# Revit family: 305_40080496f50843ed95814908d8aeb8
name_source: partatom
category: Pipe Accessories
revit_build: Autodesk Revit 2018 (Build: 20170223_1515(x64)
units: mm (PartAtom-declared; Revit-internal decimal feet)

## family parameters
Always vertical = Yes
Cut with Voids When Loaded = No
Part Type = Valve - Breaks Into
Round Connector Dimension = Use Diameter
Shared = No
Work Plane-Based = No

## types (8) — shared parameters
CAT0 = Yes
CAT0G = Yes
CATG = No
CATL = No
Description = Cast iron butterfly PN16/PN10, EPDM seat, S.S. disc
L2D = 60 mm
L2D_Min = 3048 mm
LL = 359 mm
Manufacturer = VIR
QmdConnectorList = 301;D;302;D
URL = http://www.vironline.com
VERG = Yes
VERL = No
W2D = 200 mm
magiPartTypeId = 305
magiProductFamilyId = 40080496f50843ed95814908d8aeb8

## per-type parameters (varying)
- 4025G DN200: D=200 mm; GB=73 mm; GH2=66 mm; GH3=298 mm; GH4=16 mm  [stored 0.0524934 ft]; GH4__ve=-16 mm  [stored -0.0524934 ft]; GL1=236 mm; GL2=220 mm; GL3=35 mm; GR1=145 mm; GR3=8 mm  [stored 0.0262467 ft]; H5=144 mm; H5__ve=-144 mm; HA=173 mm; HB=260 mm; L=60 mm; L1=7 mm; L2=47 mm; LH1=296 mm; LH2=36 mm; LH2__ve=-36 mm  [stored -0.11811 ft]; LH3=36 mm; LH3__ve=-36 mm  [stored -0.11811 ft]; L_2=30 mm  [stored 0.0984252 ft]; R=100 mm; R1=116 mm; R2=132 mm; R4=63 mm; R5=9 mm  [stored 0.0295276 ft]; S=14 mm  [stored 0.0459318 ft]; S__ve=-14 mm  [stored -0.0459318 ft]; W1=9 mm  [stored 0.0295276 ft]; W1__ve=-9 mm; W5=16 mm  [stored 0.0524934 ft]; magiProductId=bb37c10687674f08b1cb661799b90f
- 4025G DN250: D=250 mm; GB=73 mm; GH2=66 mm; GH3=330 mm; GH4=16 mm  [stored 0.0524934 ft]; GH4__ve=-16 mm  [stored -0.0524934 ft]; GL1=236 mm; GL2=220 mm; GL3=35 mm; GR1=145 mm; GR3=8 mm  [stored 0.0262467 ft]; H5=150 mm; H5__ve=-150 mm  [stored -0.492126 ft]; HA=203 mm; HB=292 mm; L=68 mm; L1=7 mm; L2=53 mm; LH1=328 mm; LH2=36 mm; LH2__ve=-36 mm  [stored -0.11811 ft]; LH3=36 mm; LH3__ve=-36 mm  [stored -0.11811 ft]; L_2=34 mm; R=125 mm; R1=143 mm; R2=160 mm; R4=63 mm; R5=11 mm  [stored 0.0360892 ft]; S=14 mm  [stored 0.0459318 ft]; S__ve=-14 mm  [stored -0.0459318 ft]; W1=11 mm  [stored 0.0360892 ft]; W1__ve=-11 mm  [stored -0.0360892 ft]; W5=18 mm  [stored 0.0590551 ft]; magiProductId=eb3aa0ad006548efb48d3b44f9baf8
- 4025G DN300: D=300 mm; GB=80 mm; GH2=69 mm; GH3=377 mm; GH4=17 mm  [stored 0.0557743 ft]; GH4__ve=-17 mm; GL1=231 mm; GL2=214 mm; GL3=39 mm; GR1=145 mm; GR3=9 mm  [stored 0.0295276 ft]; H5=169 mm; H5__ve=-169 mm; HA=242 mm; HB=337 mm; L=78 mm; L1=9 mm  [stored 0.0295276 ft]; L2=61 mm; LH1=373 mm; LH2=36 mm; LH2__ve=-36 mm  [stored -0.11811 ft]; LH3=36 mm; LH3__ve=-36 mm  [stored -0.11811 ft]; L_2=39 mm; R=150 mm; R1=168 mm; R2=187 mm; R4=75 mm; R5=11 mm  [stored 0.0360892 ft]; S=20 mm  [stored 0.0656168 ft]; S__ve=-20 mm  [stored -0.0656168 ft]; W1=11 mm  [stored 0.0360892 ft]; W1__ve=-11 mm  [stored -0.0360892 ft]; W5=20 mm  [stored 0.0656168 ft]; magiProductId=f7b25da7175b441aad00bf8253cd8e
- 4025G DN350: D=350 mm; GB=80 mm; GH2=69 mm; GH3=408 mm; GH4=17 mm  [stored 0.0557743 ft]; GH4__ve=-17 mm; GL1=231 mm; GL2=214 mm; GL3=39 mm; GR1=145 mm; GR3=9 mm  [stored 0.0295276 ft]; H5=173 mm; H5__ve=-173 mm  [stored -0.567585 ft]; HA=267 mm; HB=368 mm; L=78 mm; L1=9 mm  [stored 0.0295276 ft]; L2=61 mm; LH1=999 mm; LH2=631 mm; LH2__ve=-631 mm  [stored -2.07021 ft]; LH3=631 mm; LH3__ve=-631 mm  [stored -2.07021 ft]; L_2=39 mm; R=175 mm; R1=195 mm; R2=215 mm; R4=75 mm; R5=12 mm  [stored 0.0393701 ft]; S=20 mm  [stored 0.0656168 ft]; S__ve=-20 mm  [stored -0.0656168 ft]; W1=12 mm  [stored 0.0393701 ft]; W1__ve=-12 mm  [stored -0.0393701 ft]; W5=20 mm  [stored 0.0656168 ft]; magiProductId=667e2aef51be4d01b7ff7ff079f280
- 4025G DN400: D=400 mm; GB=111 mm; GH2=236 mm; GH3=535 mm; GH4=59 mm; GH4__ve=-59 mm  [stored -0.19357 ft]; GL1=243 mm; GL2=184 mm; GL3=49 mm; GR1=145 mm; GR3=30 mm  [stored 0.0984252 ft]; H5=179 mm; H5__ve=-179 mm; HA=298 mm; HB=400 mm; L=102 mm; L1=11 mm  [stored 0.0360892 ft]; L2=80 mm; LH1=999 mm; LH2=599 mm; LH2__ve=-599 mm  [stored -1.96522 ft]; LH3=599 mm; LH3__ve=-599 mm  [stored -1.96522 ft]; L_2=51 mm; R=200 mm; R1=221 mm; R2=242 mm; R4=105 mm; R5=14 mm  [stored 0.0459318 ft]; S=20 mm  [stored 0.0656168 ft]; S__ve=-20 mm  [stored -0.0656168 ft]; W1=14 mm  [stored 0.0459318 ft]; W1__ve=-14 mm  [stored -0.0459318 ft]; W5=27 mm; magiProductId=968c1d0fc5c44531849b7297465cfa
- 4025G DN450: D=450 mm; GB=111 mm; GH2=236 mm; GH3=557 mm; GH4=59 mm; GH4__ve=-59 mm  [stored -0.19357 ft]; GL1=243 mm; GL2=184 mm; GL3=49 mm; GR1=145 mm; GR3=30 mm  [stored 0.0984252 ft]; H5=175 mm; H5__ve=-175 mm; HA=318 mm; HB=422 mm; L=114 mm; L1=13 mm; L2=89 mm; LH1=999 mm; LH2=577 mm; LH2__ve=-577 mm  [stored -1.89304 ft]; LH3=577 mm; LH3__ve=-577 mm  [stored -1.89304 ft]; L_2=57 mm; R=225 mm; R1=248 mm; R2=270 mm; R4=105 mm; R5=14 mm  [stored 0.0459318 ft]; S=20 mm  [stored 0.0656168 ft]; S__ve=-20 mm  [stored -0.0656168 ft]; W1=14 mm  [stored 0.0459318 ft]; W1__ve=-14 mm  [stored -0.0459318 ft]; W5=30 mm  [stored 0.0984252 ft]; magiProductId=e49c6ee3ad524b96a637721905a74a
- 4025G DN500: D=500 mm; GB=111 mm; GH2=236 mm; GH3=614 mm; GH4=59 mm; GH4__ve=-59 mm  [stored -0.19357 ft]; GL1=243 mm; GL2=184 mm; GL3=49 mm; GR1=145 mm; GR3=30 mm  [stored 0.0984252 ft]; H5=204 mm; H5__ve=-204 mm  [stored -0.669291 ft]; HA=349 mm; HB=479 mm; L=127 mm; L1=14 mm  [stored 0.0459318 ft]; L2=99 mm; LH1=999 mm; LH2=520 mm; LH2__ve=-520 mm  [stored -1.70604 ft]; LH3=520 mm; LH3__ve=-520 mm  [stored -1.70604 ft]; L_2=64 mm; R=250 mm; R1=275 mm; R2=300 mm; R4=105 mm; R5=16 mm  [stored 0.0524934 ft]; S=22 mm  [stored 0.0721785 ft]; S__ve=-22 mm  [stored -0.0721785 ft]; W1=16 mm  [stored 0.0524934 ft]; W1__ve=-16 mm  [stored -0.0524934 ft]; W5=33 mm; magiProductId=109b4235ce73478ba31c5f0e1b1b11
- 4025G DN600: D=600 mm; GB=133 mm; GH2=267 mm; GH3=715 mm; GH4=67 mm; GH4__ve=-67 mm; GL1=296 mm; GL2=229 mm; GL3=60 mm; GR1=188 mm; GR3=33 mm; H5=234 mm; H5__ve=-234 mm; HA=410 mm; HB=562 mm; L=154 mm; L1=17 mm  [stored 0.0557743 ft]; L2=120 mm; LH1=999 mm; LH2=437 mm; LH2__ve=-437 mm  [stored -1.43373 ft]; LH3=437 mm; LH3__ve=-437 mm  [stored -1.43373 ft]; L_2=77 mm; R=300 mm; R1=328 mm; R2=357 mm; R4=105 mm; R5=18 mm  [stored 0.0590551 ft]; S=22 mm  [stored 0.0721785 ft]; S__ve=-22 mm  [stored -0.0721785 ft]; W1=18 mm  [stored 0.0590551 ft]; W1__ve=-18 mm  [stored -0.0590551 ft]; W5=40 mm; magiProductId=95a4d7f1f14e4421a584f80a65b672

note: column(s) folded — value = type name in every type: MC Product Code

note: [stored X ft] marks values corroborated as IEEE doubles in the binary element streams (Revit-internal decimal feet)

## geometry (parser evidence)
native form markers: Sweep x1
no freeform markers — native parametric forms only
